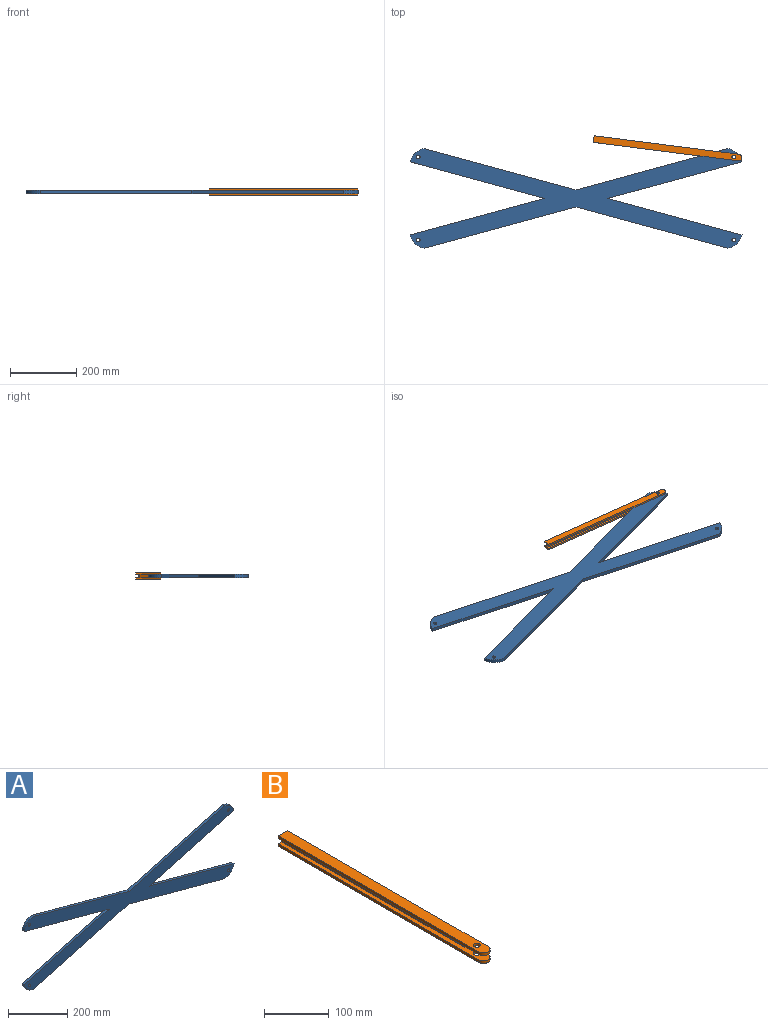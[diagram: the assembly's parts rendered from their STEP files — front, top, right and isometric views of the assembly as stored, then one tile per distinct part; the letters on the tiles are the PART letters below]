
ASSEMBLY  parts=2 mates=1
PART A: 18 faces, bbox 1000x10x300 mm
  f0: plane 456.54x124.09mm, normal (-0.26,0,0.96), area 4731mm2, adj f1,f8,f9,f14
  f1: plane 455.72x123.87mm, normal (0.26,0,0.96), area 4722.5mm2, adj f0,f8,f9,f17
  f2: plane 404.69x110mm, normal (-0.26,0,-0.96), area 4193.7mm2, adj f3,f8,f9,f17
  f3: plane 403.81x109.76mm, normal (-0.26,0,0.96), area 4184.6mm2, adj f2,f8,f9,f16
  f4: plane 456.54x124.09mm, normal (0.26,0,-0.96), area 4731mm2, adj f5,f8,f9,f16
  f5: plane 455.72x123.87mm, normal (-0.26,0,-0.96), area 4722.5mm2, adj f4,f8,f9,f15
  f6: plane 404.69x110mm, normal (0.26,0,0.96), area 4193.7mm2, adj f7,f8,f9,f15
  f7: plane 403.81x109.76mm, normal (0.26,0,-0.96), area 4184.6mm2, adj f6,f8,f9,f14
  f8: plane 1000x300mm, normal (0,-1,0), area 95269.9mm2, adj f0,f1,f2,f3,f4,f5,f6,f7
  f9: plane 1000x300mm, normal (0,1,0), area 95269.9mm2, adj f0,f1,f2,f3,f4,f5,f6,f7
  f10: cylinder r=5.5mm len=11mm, axis (0,-1,0), area 345.6mm2, adj f8,f9
  f11: cylinder r=5.5mm len=11mm, axis (0,-1,0), area 345.6mm2, adj f8,f9
  f12: cylinder r=5.5mm len=11mm, axis (0,-1,0), area 345.6mm2, adj f8,f9
  f13: cylinder r=5.5mm len=11mm, axis (0,-1,0), area 345.6mm2, adj f8,f9
  f14: cylinder r=50mm len=42.59mm, axis (0,-1,0), area 626mm2, adj f0,f7,f8,f9
  f15: cylinder r=50mm len=44.28mm, axis (0,-1,0), area 637.6mm2, adj f5,f6,f8,f9
  f16: cylinder r=50mm len=42.59mm, axis (0,1,0), area 626mm2, adj f3,f4,f8,f9
  f17: cylinder r=50mm len=44.28mm, axis (0,-1,0), area 637.6mm2, adj f1,f2,f8,f9
PART B: 16 faces, bbox 20x450x20 mm
  f0: plane 400x10mm, normal (-1,0,0), area 4000mm2, adj f1,f6,f10,f11
  f1: plane 450x20mm, normal (0,0,1), area 6862mm2, adj f0,f2,f4,f5,f10,f11,f13,f15
  f2: plane 440x5mm, normal (-1,0,0), area 2200mm2, adj f1,f3,f10,f15
  f3: plane 450x20mm, normal (0,0,-1), area 8862mm2, adj f2,f4,f10,f13,f15
  f4: plane 440x5mm, normal (1,0,0), area 2200mm2, adj f1,f3,f10,f15
  f5: plane 400x10mm, normal (1,0,0), area 4000mm2, adj f1,f6,f10,f11
  f6: plane 450x20mm, normal (0,0,-1), area 6862mm2, adj f0,f5,f7,f9,f10,f11,f12,f14
  f7: plane 440x5mm, normal (1,0,0), area 2200mm2, adj f6,f8,f10,f14
  f8: plane 450x20mm, normal (0,0,1), area 8862mm2, adj f7,f9,f10,f12,f14
  f9: plane 440x5mm, normal (-1,0,0), area 2200mm2, adj f6,f8,f10,f14
  f10: plane 20x20mm, normal (0,1,0), area 250mm2, adj f0,f1,f2,f3,f4,f5,f6,f7
  f11: plane 10x5mm, normal (0,-1,0), area 50mm2, adj f0,f1,f5,f6
  f12: cylinder r=5.5mm len=11mm, axis (0,0,1), area 172.8mm2, adj f6,f8
  f13: cylinder r=5.5mm len=11mm, axis (0,0,1), area 172.8mm2, adj f1,f3
  f14: cylinder r=10mm len=20mm, axis (0,0,1), area 157.1mm2, adj f6,f7,f8,f9
  f15: cylinder r=10mm len=20mm, axis (0,0,-1), area 157.1mm2, adj f1,f2,f3,f4
PLACE A rot(axis=(-1,0,0),90deg) t=(0,0,-10)mm fixed
PLACE B rot(axis=(0,0,1),82.7deg) t=(276.61,150.32,-5)mm
MATE revolute B.f12 <-> A.f10  axis (0,0,-1) through (475,125,0)mm
